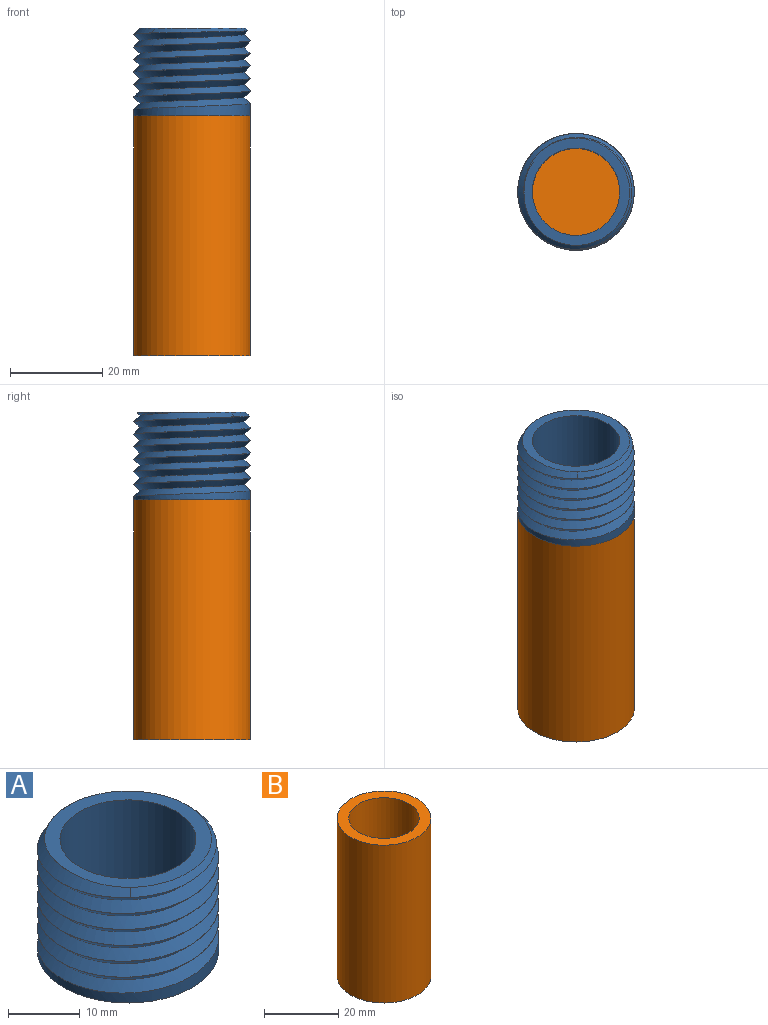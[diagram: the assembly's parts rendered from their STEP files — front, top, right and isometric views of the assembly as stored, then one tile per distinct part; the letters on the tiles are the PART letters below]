
ASSEMBLY  parts=2 mates=1
PART A: 8 faces, bbox 25.5x29.4x21 mm
  f0: cylinder r=9.48mm len=19mm, axis (0,0,-1), area 1131.1mm2, adj f2,f3
  f1: cylinder r=12.62mm len=25.25mm, axis (0,0,-1), area -6mm2, adj f3,f4,f5,f6,f7
  f2: plane 23.47x23.15mm, normal (0,0,1), area 139.3mm2, adj f0,f4,f6,f7
  f3: plane 25.25x25.25mm, normal (0,0,-1), area 218.7mm2, adj f0,f1
  f4: cone r=11.62mm half-angle=45deg, axis (0,0,-1), area 40.3mm2, adj f1,f2,f6,f7
  f5: plane 2.69x1.35mm, normal (0,1,0), area 1.8mm2, adj f1,f6,f7
  f6: bspline ~29.16x25.25mm, area 878.9mm2, adj f1,f2,f4,f5,f7
  f7: bspline ~29.16x25.25mm, area 938.5mm2, adj f1,f2,f4,f5,f6
PART B: 5 faces, bbox 25.3x25.3x52 mm
  f0: plane 18.95x18.95mm, normal (0,0,1), area 282mm2, adj f1
  f1: cylinder r=9.48mm len=49mm, axis (0,0,-1), area 2917.1mm2, adj f0,f3
  f2: cylinder r=12.62mm len=52mm, axis (0,0,-1), area 4124.9mm2, adj f3,f4
  f3: plane 25.25x25.25mm, normal (0,0,1), area 218.7mm2, adj f1,f2
  f4: plane 25.25x25.25mm, normal (0,0,-1), area 500.7mm2, adj f2
PLACE A t=(0,0,8.7)mm
PLACE B t=(0,0,8.7)mm
MATE planar B.f1 <-> A.f0  axis (0,0,1) through (0,0,60.7)mm
